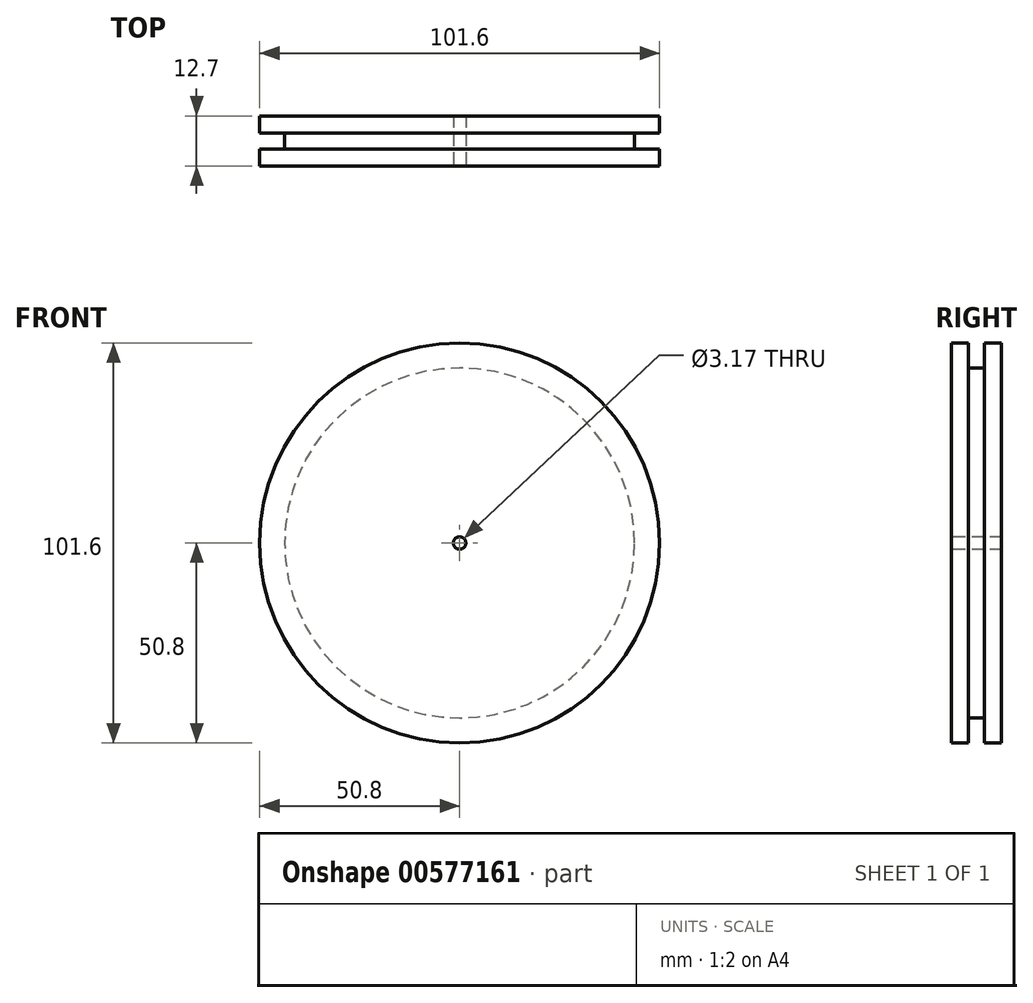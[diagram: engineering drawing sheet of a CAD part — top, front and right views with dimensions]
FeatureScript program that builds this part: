
annotation { "Feature Type Name" : "Feature", "Feature Type Description" : "" }
export const myFeature = defineFeature(function(context is Context, id is Id, definition is map)
    precondition{}
    {
        {
            var Q0;
            Q0=qCreatedBy(makeId("Right.planeOp"),FACE);
            var sketch = newSketch(context, id + "F0", { "sketchPlane" : qUnion([Q0])});
            skLineSegment(sketch, "E0", {"start": v(0, 0) * mm, "end": v(12.7, 0) * mm});
            skLineSegment(sketch, "E1", {"start": v(12.7, 0) * mm, "end": v(12.7, 50.8) * mm});
            skLineSegment(sketch, "E2", {"start": v(12.7, 50.8) * mm, "end": v(8.38, 50.8) * mm});
            skLineSegment(sketch, "E3", {"start": v(8.38, 50.8) * mm, "end": v(8.38, 44.45) * mm});
            skLineSegment(sketch, "E4", {"start": v(8.38, 44.45) * mm, "end": v(4.32, 44.45) * mm});
            skLineSegment(sketch, "E5", {"start": v(4.32, 44.45) * mm, "end": v(4.32, 50.8) * mm});
            skLineSegment(sketch, "E6", {"start": v(4.32, 50.8) * mm, "end": v(0, 50.8) * mm});
            skLineSegment(sketch, "E7", {"start": v(0, 50.8) * mm, "end": v(0, 0) * mm});
            skSolve(sketch);
        }
        {
            var Q0;
            Q0=makeQuery(id+"F0.imprint","IMPRINT",FACE,{"disambiguationData":[TD([[makeQuery(id+"F0.imprint","IMPRINT",EDGE,{"derivedFrom":sQuery(id+"F0.wireOp",EDGE,"E0")}),1.0]])]});
            var Q1;
            Q1 = qConstructionFilter(qBodyType(qCreatedBy(id + "F0" ,EDGE), BodyType.WIRE), ConstructionObject.NO);
            var Q2;
            Q2=sQuery(id+"F0.wireOp",EDGE,"E0");
            revolve(context, id + "F1", {"entities" : qUnion([Q0]), "surfaceEntities" : qUnion([Q1]), "axis" : qUnion([Q2]), "revolveType" : RevolveType.FULL});
        }
        {
            var Q0;
            Q0=makeQuery(id+"F1.opRevolve","SWEPT_FACE",FACE,{"disambiguationData":[OSD([sQuery(id+"F0.wireOp",EDGE,"E7")])]});
            var sketch = newSketch(context, id + "F2", { "sketchPlane" : qUnion([Q0])});
            skCircle(sketch, "E8", {"center": v(0, 0) * mm, "radius": 1.59 * mm});
            skSolve(sketch);
        }
        {
            var Q0;
            Q0=makeQuery(id+"F2.imprint","IMPRINT",FACE,{"disambiguationData":[TD([[makeQuery(id+"F2.imprint","IMPRINT",EDGE,{"derivedFrom":sQuery(id+"F2.wireOp",EDGE,"E8")}),1.0]])]});
            var Q1;
            Q1=sQuery(id+"F2.wireOp",EDGE,"E8");
            extrude(context, id + "F3", {"entities" : qUnion([Q0]), "operationType" : NewBodyOperationType.REMOVE, "surfaceEntities" : qUnion([Q1]), "endBound" : BoundingType.THROUGH_ALL, "oppositeDirection" : true, "depth" : 25.4 * mm, "offsetDistance" : 25.4 * mm});
        }
    });
